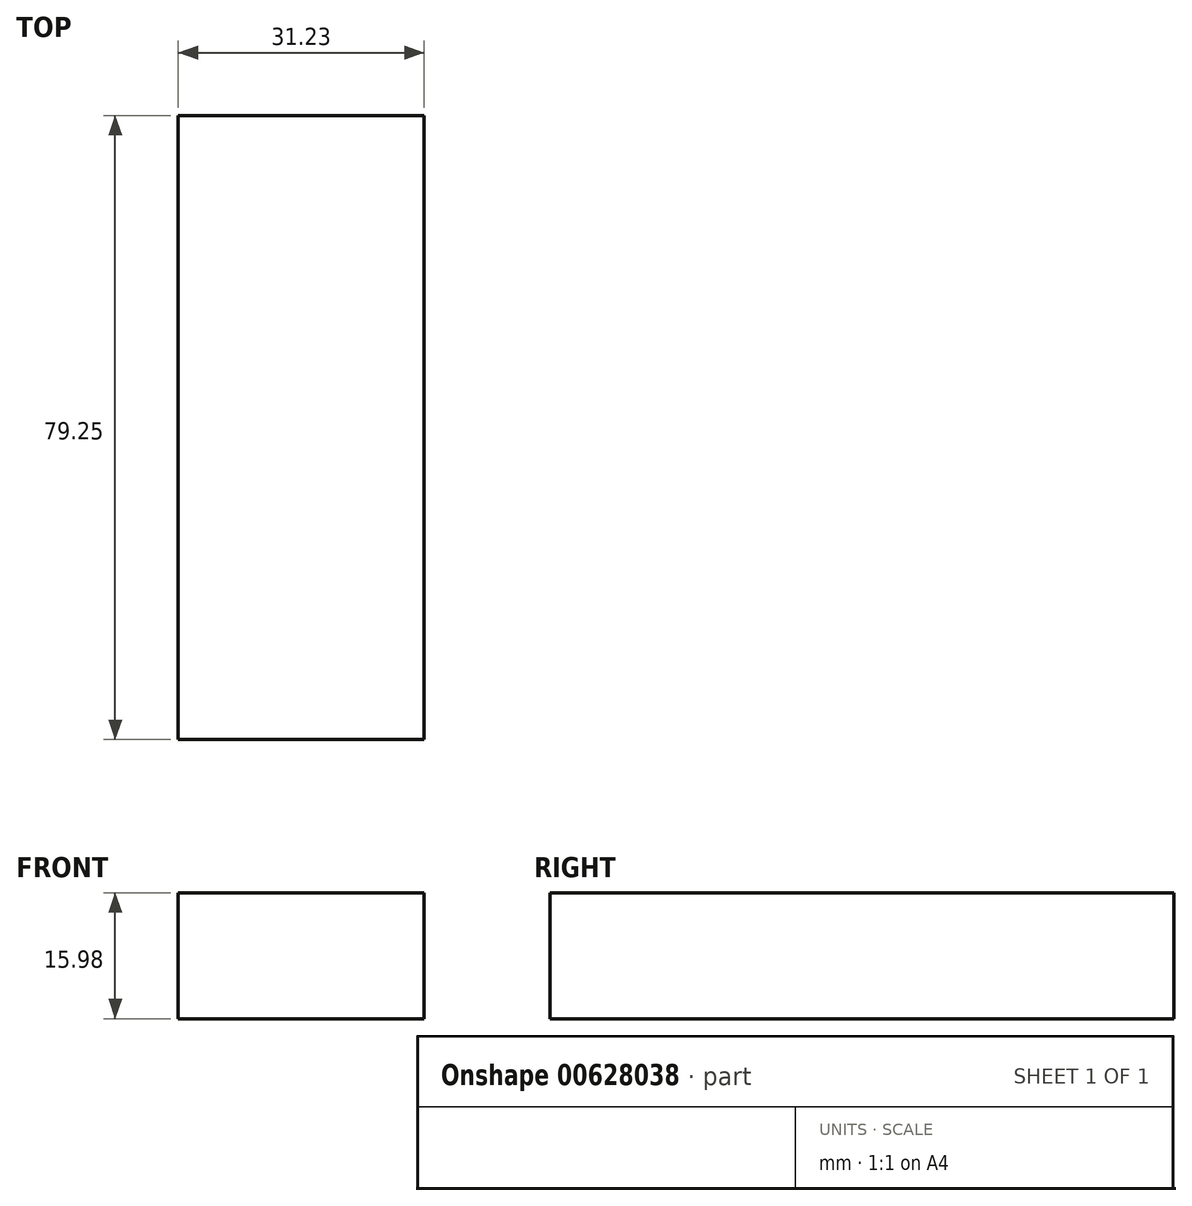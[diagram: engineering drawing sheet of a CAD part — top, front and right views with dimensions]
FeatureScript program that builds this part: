
annotation { "Feature Type Name" : "Feature", "Feature Type Description" : "" }
export const myFeature = defineFeature(function(context is Context, id is Id, definition is map)
    precondition{}
    {
        {
            var Q0;
            Q0=qCreatedBy(makeId("Front.planeOp"),FACE);
            var sketch = newSketch(context, id + "F0", { "sketchPlane" : qUnion([Q0])});
            skLineSegment(sketch, "E0.bottom", {"start": v(0, 0) * mm, "end": v(-31.23, 0) * mm});
            skLineSegment(sketch, "E0.top", {"start": v(0, 15.98) * mm, "end": v(-31.23, 15.98) * mm});
            skLineSegment(sketch, "E0.left", {"start": v(0, 0) * mm, "end": v(0, 15.98) * mm});
            skLineSegment(sketch, "E0.right", {"start": v(-31.23, 0) * mm, "end": v(-31.23, 15.98) * mm});
            skSolve(sketch);
        }
        {
            var Q0;
            Q0 = qSketchRegion(id + "F0", true);
            extrude(context, id + "F1", {"entities" : qUnion([Q0]), "depth" : 79.25 * mm, "offsetDistance" : 25.4 * mm});
        }
    });
